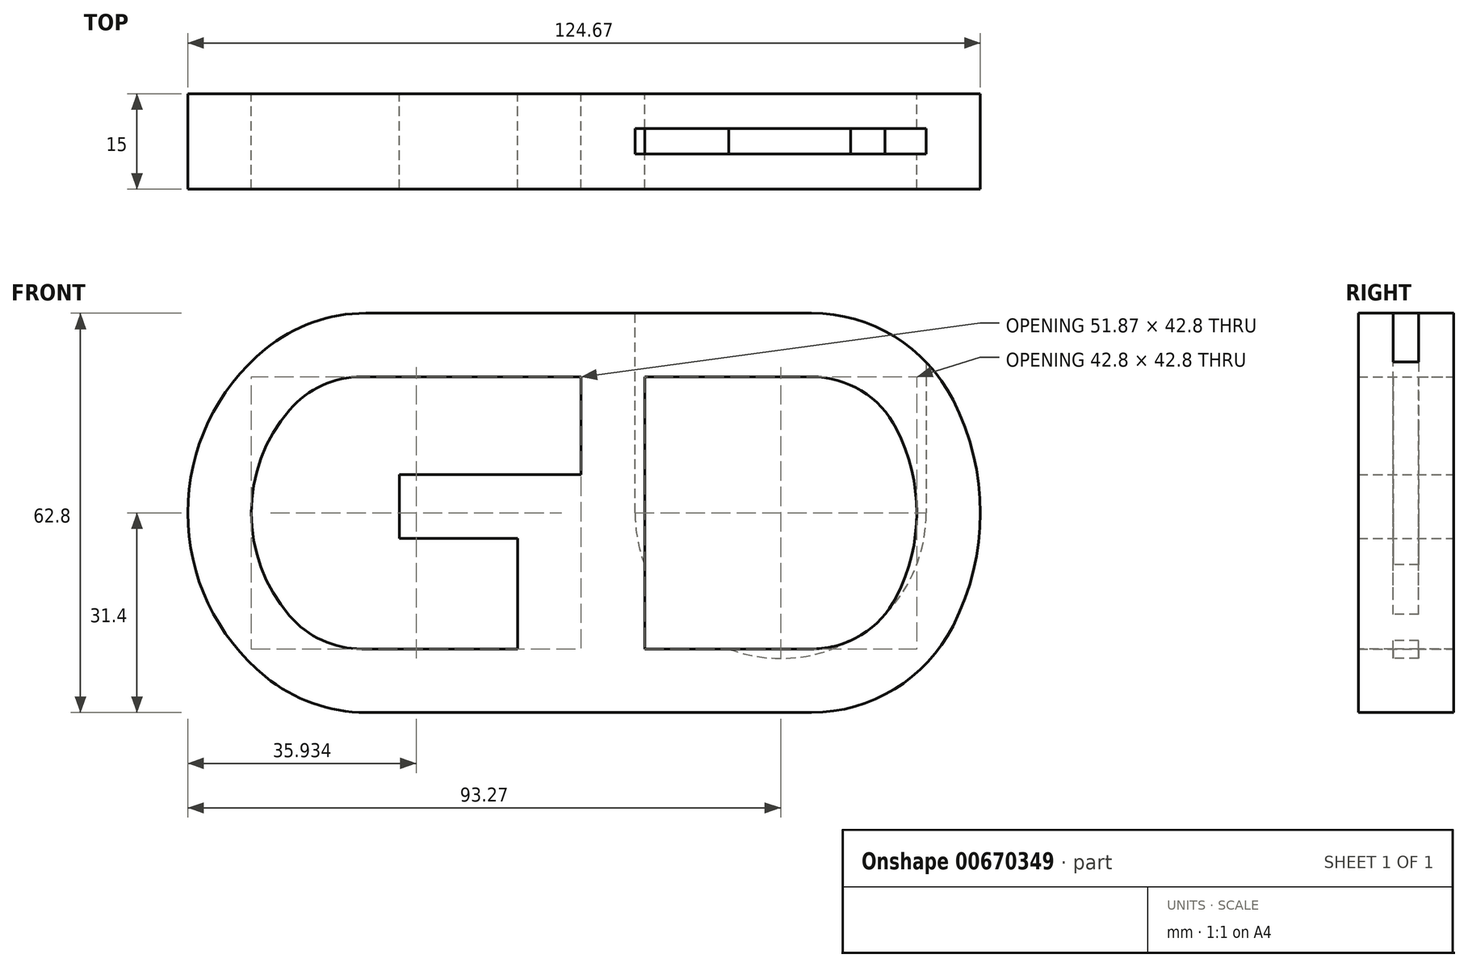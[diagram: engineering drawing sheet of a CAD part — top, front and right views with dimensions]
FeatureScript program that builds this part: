
annotation { "Feature Type Name" : "Feature", "Feature Type Description" : "" }
export const myFeature = defineFeature(function(context is Context, id is Id, definition is map)
    precondition{}
    {
        {
            var Q0;
            Q0=qCreatedBy(makeId("Front.planeOp"),FACE);
            var sketch = newSketch(context, id + "F0", { "sketchPlane" : qUnion([Q0])});
            skCircle(sketch, "E0", {"center": v(0, 0) * mm, "radius": 22.4 * mm, "construction": true});
            skLineSegment(sketch, "E1", {"start": v(-21.4, 21.4) * mm, "end": v(-21.4, -21.4) * mm});
            skLineSegment(sketch, "E2", {"start": v(-21.4, 21.4) * mm, "end": v(12, 21.4) * mm});
            skLineSegment(sketch, "E3", {"start": v(-21.4, -21.4) * mm, "end": v(12, -21.4) * mm});
            skLineSegment(sketch, "E4.0", {"start": v(-31.4, 31.4) * mm, "end": v(15.57, 31.4) * mm});
            skLineSegment(sketch, "E4.1", {"start": v(-31.4, 31.4) * mm, "end": v(-31.4, -31.4) * mm});
            skLineSegment(sketch, "E4.2", {"start": v(-31.4, -31.4) * mm, "end": v(15.57, -31.4) * mm});
            skArc(sketch, "E5", {"start": v(12, -21.4) * mm, "mid": v(21.4, 0) * mm, "end": v(12, 21.4) * mm});
            skArc(sketch, "E6", {"start": v(-31.4, -31.02) * mm, "mid": v(-31.15, -31.2) * mm, "end": v(-30.9, -31.4) * mm});
            skArc(sketch, "E7.trimOffspring", {"start": v(15.57, -31.4) * mm, "mid": v(31.4, 0) * mm, "end": v(15.57, 31.4) * mm});
            skSolve(sketch);
        }
        {
            var Q0;
            Q0 = qSketchRegion(id + "F0", true);
            extrude(context, id + "F1", {"entities" : qUnion([Q0]), "endBound" : BoundingType.SYMMETRIC, "depth" : 15 * mm, "offsetDistance" : 25 * mm});
        }
        {
            var Q0;
            Q0=qCreatedBy(makeId("Front.planeOp"),FACE);
            var sketch = newSketch(context, id + "F2", { "sketchPlane" : qUnion([Q0])});
            skLineSegment(sketch, "E8", {"start": v(-71, -31.4) * mm, "end": v(-31.4, -31.4) * mm});
            skPoint(sketch, "E9.visualSharp", {"position": v(-28, -31.4) * mm});
            skArc(sketch, "E10", {"start": v(-71, 31.4) * mm, "mid": v(-93.27, 0) * mm, "end": v(-71, -31.4) * mm});
            skLineSegment(sketch, "E11", {"start": v(-71, 31.4) * mm, "end": v(-31.4, 31.4) * mm});
            skLineSegment(sketch, "E12", {"start": v(-31.4, 6) * mm, "end": v(-60, 6) * mm});
            skPoint(sketch, "E13.visualSharp", {"position": v(-28, 31.4) * mm});
            skPoint(sketch, "E14.visualSharp", {"position": v(-28, 6) * mm});
            skLineSegment(sketch, "E15.0", {"start": v(-41.4, -4) * mm, "end": v(-60, -4) * mm});
            skLineSegment(sketch, "E15.2", {"start": v(-41.4, -21.4) * mm, "end": v(-41.4, -4) * mm});
            skLineSegment(sketch, "E15.5", {"start": v(-71, 21.4) * mm, "end": v(-31.4, 21.4) * mm});
            skArc(sketch, "E15.6", {"start": v(-71, 21.4) * mm, "mid": v(-83.27, 0) * mm, "end": v(-71, -21.4) * mm});
            skLineSegment(sketch, "E15.7", {"start": v(-71, -21.4) * mm, "end": v(-41.4, -21.4) * mm});
            skLineSegment(sketch, "E16", {"start": v(-60, 6) * mm, "end": v(-60, -4) * mm});
            skLineSegment(sketch, "E17.0", {"start": v(-31.4, 31.4) * mm, "end": v(-31.4, 21.4) * mm});
            skLineSegment(sketch, "E18.trimOffspring", {"start": v(-31.4, 6) * mm, "end": v(-31.4, -31.4) * mm});
            skSolve(sketch);
        }
        {
            var Q0;
            Q0 = qSketchRegion(id + "F2", true);
            extrude(context, id + "F3", {"entities" : qUnion([Q0]), "operationType" : NewBodyOperationType.ADD, "endBound" : BoundingType.SYMMETRIC, "depth" : 15 * mm, "offsetDistance" : 25 * mm});
        }
        {
            var Q0;
            Q0=makeQuery(id+"F3.opExtrude","SWEPT_EDGE",EDGE,{"disambiguationData":[OSD([sQuery(id+"F2.wireOp",EDGE,"E15.5"),sQuery(id+"F2.wireOp",EDGE,"E15.6")])]});
            var Q1;
            Q1=makeQuery(id+"F3.opExtrude","SWEPT_EDGE",EDGE,{"disambiguationData":[OSD([sQuery(id+"F2.wireOp",EDGE,"E15.6"),sQuery(id+"F2.wireOp",EDGE,"E15.7")])]});
            var Q2;
            Q2=makeQuery(id+"F1.opExtrude","SWEPT_EDGE",EDGE,{"disambiguationData":[OSD([sQuery(id+"F0.wireOp",EDGE,"E3"),sQuery(id+"F0.wireOp",EDGE,"E5")])]});
            var Q3;
            Q3=makeQuery(id+"F1.opExtrude","SWEPT_EDGE",EDGE,{"disambiguationData":[OSD([sQuery(id+"F0.wireOp",EDGE,"E2"),sQuery(id+"F0.wireOp",EDGE,"E5")])]});
            fillet(context, id + "F4", {"entities" : qUnion([Q0, Q1, Q2, Q3]), "radius" : 15 * mm, "tangentPropagation" : true, "allowEdgeOverflow" : false});
        }
        {
            var Q0;
            Q0=makeQuery(id+"F3.opExtrude","SWEPT_EDGE",EDGE,{"disambiguationData":[OSD([sQuery(id+"F2.wireOp",EDGE,"E10"),sQuery(id+"F2.wireOp",EDGE,"E11")])]});
            var Q1;
            Q1=makeQuery(id+"F3.opExtrude","SWEPT_EDGE",EDGE,{"disambiguationData":[OSD([sQuery(id+"F2.wireOp",EDGE,"E8"),sQuery(id+"F2.wireOp",EDGE,"E10")])]});
            var Q2;
            Q2=makeQuery(id+"F1.opExtrude","SWEPT_EDGE",EDGE,{"disambiguationData":[OSD([sQuery(id+"F0.wireOp",EDGE,"E4.2"),sQuery(id+"F0.wireOp",EDGE,"E7.trimOffspring")])]});
            var Q3;
            Q3=makeQuery(id+"F1.opExtrude","SWEPT_EDGE",EDGE,{"disambiguationData":[OSD([sQuery(id+"F0.wireOp",EDGE,"E4.0"),sQuery(id+"F0.wireOp",EDGE,"E7.trimOffspring")])]});
            fillet(context, id + "F5", {"entities" : qUnion([Q0, Q1, Q2, Q3]), "radius" : 25 * mm, "tangentPropagation" : true, "allowEdgeOverflow" : false});
        }
        {
            var Q0;
            Q0=qCreatedBy(makeId("Front.planeOp"),FACE);
            var sketch = newSketch(context, id + "F6", { "sketchPlane" : qUnion([Q0])});
            skArc(sketch, "E19", {"start": v(-22.9, 0) * mm, "mid": v(0, -22.9) * mm, "end": v(22.9, 0) * mm});
            skLineSegment(sketch, "E20", {"start": v(-22.9, 0) * mm, "end": v(-22.9, 35.19) * mm});
            skLineSegment(sketch, "E21", {"start": v(-22.9, 35.19) * mm, "end": v(22.9, 35.19) * mm});
            skLineSegment(sketch, "E22", {"start": v(22.9, 35.19) * mm, "end": v(22.9, 0) * mm});
            skSolve(sketch);
        }
        {
            var Q0;
            Q0 = qSketchRegion(id + "F6", true);
            extrude(context, id + "F7", {"entities" : qUnion([Q0]), "operationType" : NewBodyOperationType.REMOVE, "endBound" : BoundingType.SYMMETRIC, "oppositeDirection" : true, "depth" : 4 * mm, "offsetDistance" : 25 * mm});
        }
    });
